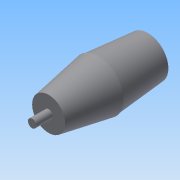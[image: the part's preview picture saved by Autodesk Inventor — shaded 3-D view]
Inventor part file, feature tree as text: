
AUTODESK INVENTOR PART (.ipt)
format: ipt  version: 2015 (Build 190159000, 159)  size: 96,768 bytes
history: native  units: mm
features: sketch x4, extrude x3
ambient origin geometry x8: Origin, YZ Plane, XZ Plane, XY Plane, X Axis, Y Axis, Z Axis, Center Point
bodies: Solid1 (feature_tree)
feature tree (7):
  extrude  "Extrusion1"  Depth=30.0mm
  sketch  "Sketch2"  dims[d3=30.0mm d4=30.0mm d5=-0.872665mm]
  extrude  "Extrusion2"  Depth=30.0mm
  extrude  "Extrusion3"  Depth=10.0mm TaperAngle=0.0deg
  sketch  "Sketch1"  dims[d0=20.0mm d1=30.0mm d2=1.745329mm]
  sketch  "Sketch3"  dims[d6=5.0mm d7=10.0mm d8=0.0mm]
  sketch  "Sketch4"
